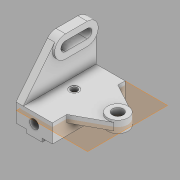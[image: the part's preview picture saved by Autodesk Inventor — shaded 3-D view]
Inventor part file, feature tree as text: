
AUTODESK INVENTOR PART (.ipt)
format: ipt  version: 2020 (Build 240168000, 168)  size: 215,552 bytes
history: native  units: mm
features: sketch x10, extrude x8, plane x1, hole x1
ambient origin geometry x8: Origin, YZ Plane, XZ Plane, XY Plane, X Axis, Y Axis, Z Axis, Center Point
bodies: Solid1 (feature_tree)
feature tree (20):
  extrude  "Extrusion1"  Depth=22.0mm
  extrude  "Extrusion2"  Depth=30.0mm
  extrude  "Extrusion3"  Depth=55.0mm
  plane  "Work Plane1"
  extrude  "Extrusion4"  Depth=45.0mm
  extrude  "Extrusion5"  Depth=10.0mm
  sketch  "Sketch6"  dims[d16=14.0mm d17=35.0mm]
  extrude  "AgujeroSuperior"  Depth=35.0mm
  extrude  "AgujeroFrontal"  Depth=10.0mm TaperAngle=0.0deg
  extrude  "AgujeroCirculo"  Depth=16.0mm TaperAngle=0.0deg
  hole  "Agujero1"  [1 undecoded]
  sketch  "Sketch1"  dims[d0=50.0mm d2=22.0mm]
  sketch  "Sketch2"  dims[d4=4.8mm d5=30.0mm]
  sketch  "Sketch3"  dims[d6=100.0mm d7=0.0mm d9=55.0mm]
  sketch  "Sketch4"  dims[d10=15.0mm d11=45.0mm]
  sketch  "Sketch5"  dims[d12=10.0mm d13=0.0mm d15=55.0mm]
  sketch  "Boceto7"  dims[d18=85.0mm d19=10.0mm d20=0.0mm]
  sketch  "Boceto8"  dims[d21=-5.0mm d22=16.0mm d23=0.0mm]
  sketch  "Boceto10"  dims[d24=30.0mm d25=3.0mm d26=0.0mm]
  sketch  "Boceto11"  dims[d27=15.0mm d30=30.0mm d31=13.0mm d32=0.0mm d33=55.0mm d35=12.7mm d37=12.5mm d38=11.0mm d39=16.0mm d40=100.0mm d41=0.0mm d47=15.0mm d48=28.0mm d49=16.0mm d50=0.0mm d52=13.0mm d53=25.0mm d54=35.0mm d55=9.0mm d56=6.0mm d57=13.0mm d58=0.3mm d59=90.0deg d60=8.0mm d61=20.594885mm]
note: 1 required parameter value undecoded (feature->parameter linkage not recoverable at this tier; creation-order binding heuristic only, values carry confidence <= 0.55)
